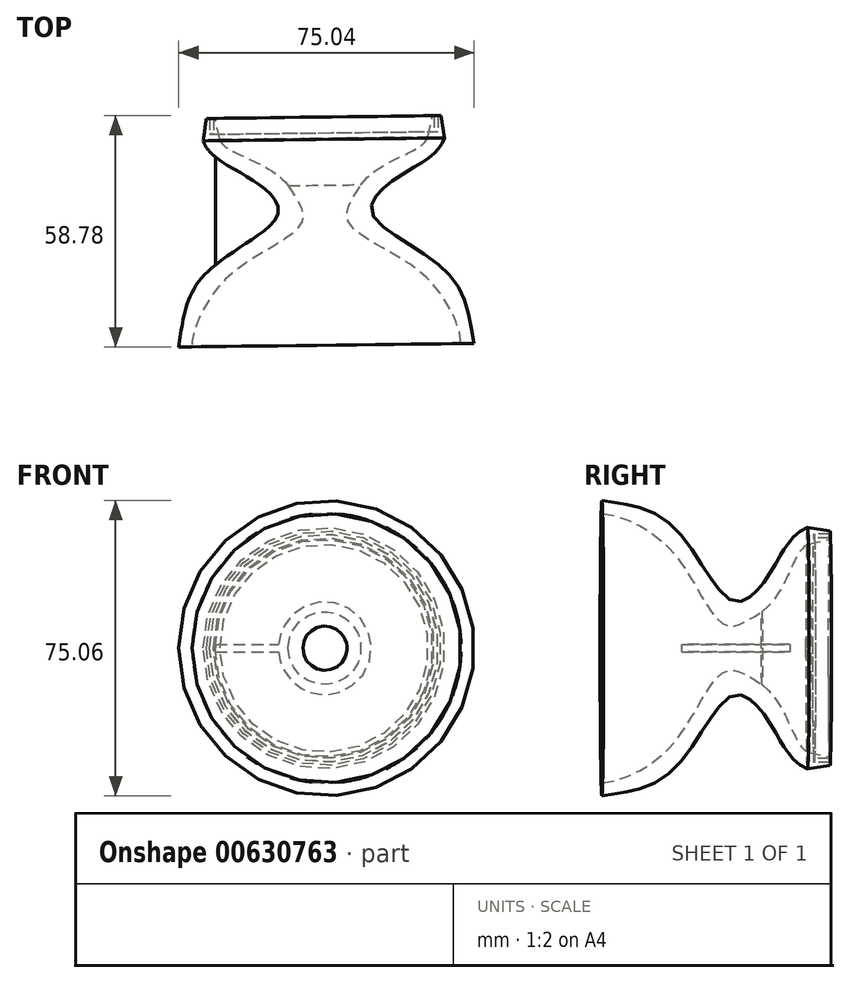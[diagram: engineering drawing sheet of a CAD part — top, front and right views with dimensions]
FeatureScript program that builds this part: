
annotation { "Feature Type Name" : "Feature", "Feature Type Description" : "" }
export const myFeature = defineFeature(function(context is Context, id is Id, definition is map)
    precondition{}
    {
        {
            var Q0;
            Q0=qCreatedBy(makeId("Top.planeOp"),FACE);
            var sketch = newSketch(context, id + "F0", { "sketchPlane" : qUnion([Q0])});
            skLineSegment(sketch, "E0", {"start": v(-29.2, 13.06) * mm, "end": v(-28.2, 13.06) * mm});
            skLineSegment(sketch, "E1", {"start": v(-28.2, 13.06) * mm, "end": v(-28.2, 17.06) * mm});
            skLineSegment(sketch, "E2", {"start": v(-29.2, 13.06) * mm, "end": v(-29.2, 17.06) * mm});
            skPoint(sketch, "E3", {"position": v(-28.2, 17.06) * mm});
            skPoint(sketch, "E4", {"position": v(-0.2, 17.06) * mm});
            skLineSegment(sketch, "E5", {"start": v(-28.2, 17.06) * mm, "end": v(-27.85, 17.06) * mm});
            skLineSegment(sketch, "E6", {"start": v(-27.85, 17.06) * mm, "end": v(-26.58, 11.76) * mm});
            skLineSegment(sketch, "E7", {"start": v(-29.2, 17.06) * mm, "end": v(-30.03, 17.06) * mm});
            skLineSegment(sketch, "E8", {"start": v(-30.03, 17.06) * mm, "end": v(-30.82, 11.36) * mm});
            skFitSpline(sketch, "E9", {"points": [v(-26.58, 11.76) * mm, v(-9.26, 0) * mm], "startDerivative": vector(3.9, -12.63) * mm, "endDerivative": vector(15.52, -20.42) * mm});
            skFitSpline(sketch, "E10", {"points": [v(-9.26, 0) * mm, v(-5.61, -8.61) * mm, v(-24.68, -23.32) * mm, v(-33.71, -40.89) * mm], "startDerivative": vector(13.88, -23.87) * mm, "endDerivative": vector(0.9, -27.34) * mm});
            skLineSegment(sketch, "E11", {"start": v(-37.03, -41) * mm, "end": v(-33.71, -40.89) * mm});
            skFitSpline(sketch, "E12", {"points": [v(-30.82, 11.36) * mm, v(-27.7, 7.23) * mm, v(-16.26, 0) * mm, v(-12, -7.7) * mm, v(-31.28, -23.53) * mm, v(-37.03, -41) * mm], "startDerivative": vector(10.44, -30.12) * mm, "endDerivative": vector(-11.5, -63.37) * mm});
            skLineSegment(sketch, "E13", {"start": v(-0.2, 17.06) * mm, "end": v(0, 0) * mm});
            skSolve(sketch);
        }
        {
            var Q0;
            Q0=makeQuery(id+"F0.imprint","IMPRINT",FACE,{"disambiguationData":[TD([[makeQuery(id+"F0.imprint","IMPRINT",EDGE,{"derivedFrom":sQuery(id+"F0.wireOp",EDGE,"E0")}),-1.0]])]});
            var Q1;
            Q1=sQuery(id+"F0.wireOp",EDGE,"E13");
            revolve(context, id + "F1", {"entities" : qUnion([Q0]), "axis" : qUnion([Q1]), "revolveType" : RevolveType.FULL});
        }
        {
            var Q0;
            Q0=qCreatedBy(makeId("Top.planeOp"),FACE);
            var sketch = newSketch(context, id + "F2", { "sketchPlane" : qUnion([Q0])});
            skLineSegment(sketch, "E14", {"start": v(-27.74, 8) * mm, "end": v(-27.74, -21.64) * mm});
            skLineSegment(sketch, "E15", {"start": v(-27.74, -21.64) * mm, "end": v(-9.09, -7.35) * mm});
            skLineSegment(sketch, "E16", {"start": v(-9.09, -7.35) * mm, "end": v(-14.72, 0) * mm});
            skLineSegment(sketch, "E17", {"start": v(-14.72, 0) * mm, "end": v(-27.74, 8) * mm});
            skSolve(sketch);
        }
        {
            var Q0;
            Q0=makeQuery(id+"F2.imprint","IMPRINT",FACE,{"disambiguationData":[TD([[makeQuery(id+"F2.imprint","IMPRINT",EDGE,{"derivedFrom":sQuery(id+"F2.wireOp",EDGE,"E14")}),1.0]])]});
            extrude(context, id + "F3", {"entities" : qUnion([Q0]), "operationType" : NewBodyOperationType.ADD, "oppositeDirection" : true, "depth" : 1 * mm, "offsetDistance" : 25 * mm, "hasSecondDirection" : true, "secondDirectionOppositeDirection" : false, "secondDirectionDepth" : 1 * mm});
        }
    });
